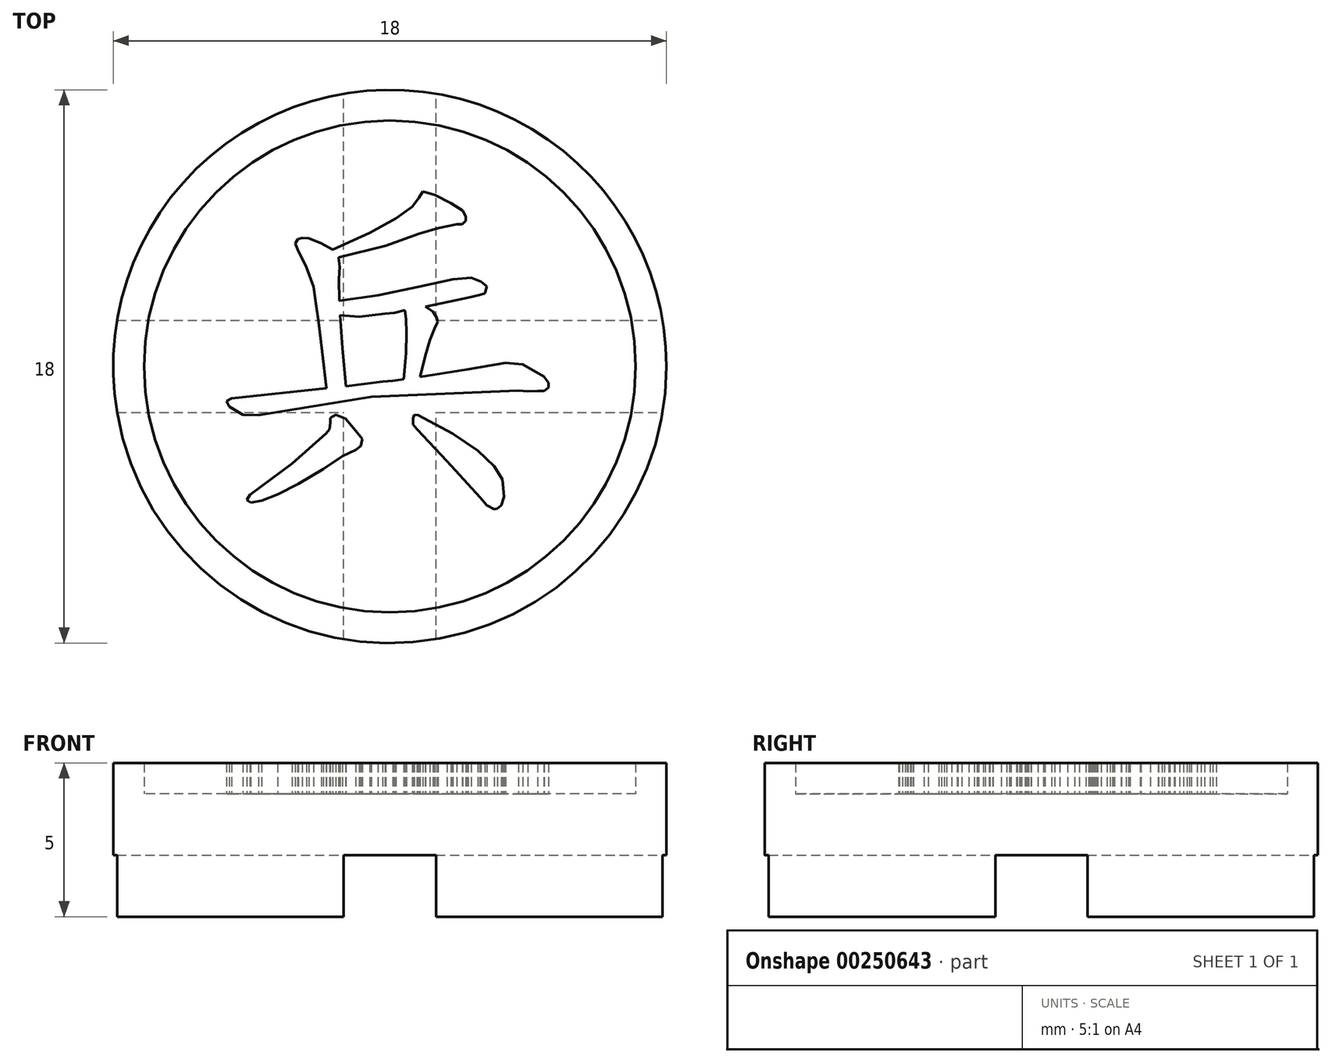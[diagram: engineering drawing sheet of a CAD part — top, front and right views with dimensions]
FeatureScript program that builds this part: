
annotation { "Feature Type Name" : "Feature", "Feature Type Description" : "" }
export const myFeature = defineFeature(function(context is Context, id is Id, definition is map)
    precondition{}
    {
        {
            var Q0;
            Q0=qCreatedBy(makeId("Top.planeOp"),FACE);
            var sketch = newSketch(context, id + "F0", { "sketchPlane" : qUnion([Q0])});
            skCircle(sketch, "E0", {"center": v(-31.33, 19.76) * mm, "radius": 9 * mm});
            skSolve(sketch);
        }
        {
            var Q0;
            Q0=qSketchRegion(id+"F0",true);
            extrude(context, id + "F1", {"entities" : qUnion([Q0]), "depth" : 4 * mm});
        }
        {
            var Q0;
            Q0=makeQuery(id+"F1.opExtrude","CAP_FACE",FACE,{"disambiguationData":[OSD([sQuery(id+"F0.wireOp",EDGE,"E0")])],"isStart":false});
            var sketch = newSketch(context, id + "F2", { "sketchPlane" : qUnion([Q0])});
            skCircle(sketch, "E1", {"center": v(-31.33, 19.76) * mm, "radius": 8 * mm});
            skCircle(sketch, "E2", {"center": v(-31.33, 19.76) * mm, "radius": 9 * mm});
            skSolve(sketch);
        }
        {
            var Q0;
            Q0=makeQuery(id+"F1.opExtrude","CAP_FACE",FACE,{"disambiguationData":[OSD([sQuery(id+"F0.wireOp",EDGE,"E0")])],"isStart":true});
            var sketch = newSketch(context, id + "F3", { "sketchPlane" : qUnion([Q0])});
            skLineSegment(sketch, "E3", {"start": v(-31.33, -19.76) * mm, "end": v(-22.33, -19.76) * mm, "construction": true});
            skLineSegment(sketch, "E4", {"start": v(-31.33, -19.76) * mm, "end": v(-31.33, -10.76) * mm, "construction": true});
            skLineSegment(sketch, "E5", {"start": v(-31.33, -19.76) * mm, "end": v(-40.33, -19.76) * mm, "construction": true});
            skLineSegment(sketch, "E6", {"start": v(-31.33, -19.76) * mm, "end": v(-31.33, -28.76) * mm, "construction": true});
            skLineSegment(sketch, "E7.bottom", {"start": v(-40.33, -28.76) * mm, "end": v(-22.33, -28.76) * mm});
            skLineSegment(sketch, "E7.top", {"start": v(-40.33, -10.76) * mm, "end": v(-22.33, -10.76) * mm});
            skLineSegment(sketch, "E7.left", {"start": v(-22.33, -10.76) * mm, "end": v(-22.33, -28.76) * mm});
            skLineSegment(sketch, "E7.right", {"start": v(-40.33, -10.76) * mm, "end": v(-40.33, -28.76) * mm});
            skPoint(sketch, "E8", {"position": v(-31.33, -28.76) * mm});
            skPoint(sketch, "E9", {"position": v(-40.33, -19.76) * mm});
            skPoint(sketch, "E10", {"position": v(-22.33, -19.76) * mm});
            skPoint(sketch, "E11", {"position": v(-31.33, -10.76) * mm});
            skLineSegment(sketch, "E12.bottom", {"start": v(-32.83, -10.76) * mm, "end": v(-29.83, -10.76) * mm});
            skLineSegment(sketch, "E12.top", {"start": v(-32.83, -28.76) * mm, "end": v(-29.83, -28.76) * mm});
            skLineSegment(sketch, "E12.left", {"start": v(-32.83, -10.76) * mm, "end": v(-32.83, -28.76) * mm});
            skLineSegment(sketch, "E12.right", {"start": v(-29.83, -10.76) * mm, "end": v(-29.83, -28.76) * mm});
            skLineSegment(sketch, "E13.bottom", {"start": v(-40.33, -18.26) * mm, "end": v(-22.33, -18.26) * mm});
            skLineSegment(sketch, "E13.top", {"start": v(-40.33, -21.26) * mm, "end": v(-22.33, -21.26) * mm});
            skLineSegment(sketch, "E13.left", {"start": v(-40.33, -18.26) * mm, "end": v(-40.33, -21.26) * mm});
            skLineSegment(sketch, "E13.right", {"start": v(-22.33, -18.26) * mm, "end": v(-22.33, -21.26) * mm});
            skSolve(sketch);
        }
        {
            var Q0;
            {var subQ1=sQuery(id+"F3.wireOp",EDGE,"E12.bottom");var subQ3=makeQuery(id+"F1.opExtrude","CAP_EDGE",EDGE,{"disambiguationData":[OSD([sQuery(id+"F0.wireOp",EDGE,"E0")])],"isStart":true});var subQ4=makeQuery(id+"F3.imprint","INTERSECT",VERTEX,{"derivedFrom":[subQ3,subQ1]});Q0=makeQuery(id+"F3.imprint","IMPRINT",FACE,{"disambiguationData":[TD([[makeQuery(id+"F3.imprint","IMPRINT",EDGE,{"disambiguationData":[TD([[subQ4,1.0]])],"derivedFrom":subQ3}),1.0]])]});}
            var Q1;
            {var subQ1=sQuery(id+"F3.wireOp",EDGE,"E12.bottom");var subQ3=makeQuery(id+"F1.opExtrude","CAP_EDGE",EDGE,{"disambiguationData":[OSD([sQuery(id+"F0.wireOp",EDGE,"E0")])],"isStart":true});var subQ4=makeQuery(id+"F3.imprint","INTERSECT",VERTEX,{"derivedFrom":[subQ3,subQ1]});Q1=makeQuery(id+"F3.imprint","IMPRINT",FACE,{"disambiguationData":[TD([[makeQuery(id+"F3.imprint","IMPRINT",EDGE,{"disambiguationData":[TD([[subQ4,-1.0]])],"derivedFrom":subQ3}),1.0]])]});}
            var Q2;
            {var subQ1=sQuery(id+"F3.wireOp",EDGE,"E12.top");var subQ3=makeQuery(id+"F1.opExtrude","CAP_EDGE",EDGE,{"disambiguationData":[OSD([sQuery(id+"F0.wireOp",EDGE,"E0")])],"isStart":true});var subQ4=makeQuery(id+"F3.imprint","INTERSECT",VERTEX,{"derivedFrom":[subQ3,subQ1]});Q2=makeQuery(id+"F3.imprint","IMPRINT",FACE,{"disambiguationData":[TD([[makeQuery(id+"F3.imprint","IMPRINT",EDGE,{"disambiguationData":[TD([[subQ4,-1.0]])],"derivedFrom":subQ3}),1.0]])]});}
            var Q3;
            {var subQ1=sQuery(id+"F3.wireOp",EDGE,"E12.top");var subQ3=makeQuery(id+"F1.opExtrude","CAP_EDGE",EDGE,{"disambiguationData":[OSD([sQuery(id+"F0.wireOp",EDGE,"E0")])],"isStart":true});var subQ4=makeQuery(id+"F3.imprint","INTERSECT",VERTEX,{"derivedFrom":[subQ3,subQ1]});Q3=makeQuery(id+"F3.imprint","IMPRINT",FACE,{"disambiguationData":[TD([[makeQuery(id+"F3.imprint","IMPRINT",EDGE,{"disambiguationData":[TD([[subQ4,1.0]])],"derivedFrom":subQ3}),1.0]])]});}
            var Q4;
            {var subQ0=sQuery(id+"F3.wireOp",EDGE,"E13.left");var subQ3=makeQuery(id+"F1.opExtrude","CAP_EDGE",EDGE,{"disambiguationData":[OSD([sQuery(id+"F0.wireOp",EDGE,"E0")])],"isStart":true});var subQ5=makeQuery(id+"F3.imprint","INTERSECT",VERTEX,{"derivedFrom":[subQ3,subQ0]});Q4=makeQuery(id+"F3.imprint","IMPRINT",FACE,{"disambiguationData":[TD([[makeQuery(id+"F3.imprint","IMPRINT",EDGE,{"disambiguationData":[TD([[subQ5,-1.0]])],"derivedFrom":subQ3}),1.0]])]});}
            var Q5;
            {var subQ0=sQuery(id+"F3.wireOp",EDGE,"E13.right");var subQ3=makeQuery(id+"F1.opExtrude","CAP_EDGE",EDGE,{"disambiguationData":[OSD([sQuery(id+"F0.wireOp",EDGE,"E0")])],"isStart":true});var subQ5=makeQuery(id+"F3.imprint","INTERSECT",VERTEX,{"derivedFrom":[subQ3,subQ0]});Q5=makeQuery(id+"F3.imprint","IMPRINT",FACE,{"disambiguationData":[TD([[makeQuery(id+"F3.imprint","IMPRINT",EDGE,{"disambiguationData":[TD([[subQ5,1.0]])],"derivedFrom":subQ3}),1.0]])]});}
            var Q6;
            {var subQ0=sQuery(id+"F3.wireOp",EDGE,"E13.left");var subQ3=makeQuery(id+"F1.opExtrude","CAP_EDGE",EDGE,{"disambiguationData":[OSD([sQuery(id+"F0.wireOp",EDGE,"E0")])],"isStart":true});var subQ5=makeQuery(id+"F3.imprint","INTERSECT",VERTEX,{"derivedFrom":[subQ3,subQ0]});Q6=makeQuery(id+"F3.imprint","IMPRINT",FACE,{"disambiguationData":[TD([[makeQuery(id+"F3.imprint","IMPRINT",EDGE,{"disambiguationData":[TD([[subQ5,1.0]])],"derivedFrom":subQ3}),1.0]])]});}
            var Q7;
            {var subQ0=sQuery(id+"F3.wireOp",EDGE,"E13.right");var subQ3=makeQuery(id+"F1.opExtrude","CAP_EDGE",EDGE,{"disambiguationData":[OSD([sQuery(id+"F0.wireOp",EDGE,"E0")])],"isStart":true});var subQ5=makeQuery(id+"F3.imprint","INTERSECT",VERTEX,{"derivedFrom":[subQ3,subQ0]});Q7=makeQuery(id+"F3.imprint","IMPRINT",FACE,{"disambiguationData":[TD([[makeQuery(id+"F3.imprint","IMPRINT",EDGE,{"disambiguationData":[TD([[subQ5,-1.0]])],"derivedFrom":subQ3}),1.0]])]});}
            var Q8;
            {var subQ3=makeQuery(id+"F1.opExtrude","CAP_EDGE",EDGE,{"disambiguationData":[OSD([sQuery(id+"F0.wireOp",EDGE,"E0")])],"isStart":true});var subQ5=sQuery(id+"F3.wireOp",EDGE,"E12.left");var subQ8=makeQuery(id+"F3.imprint","INTERSECT",VERTEX,{"disambiguationData":[OD(1.0)],"derivedFrom":[subQ3,subQ5]});Q8=makeQuery(id+"F3.imprint","IMPRINT",FACE,{"disambiguationData":[TD([[makeQuery(id+"F3.imprint","IMPRINT",EDGE,{"disambiguationData":[TD([[subQ8,-1.0]])],"derivedFrom":subQ3}),1.0]])]});}
            var Q9;
            {var subQ3=makeQuery(id+"F1.opExtrude","CAP_EDGE",EDGE,{"disambiguationData":[OSD([sQuery(id+"F0.wireOp",EDGE,"E0")])],"isStart":true});var subQ5=sQuery(id+"F3.wireOp",EDGE,"E12.right");var subQ8=makeQuery(id+"F3.imprint","INTERSECT",VERTEX,{"disambiguationData":[OD(1.0)],"derivedFrom":[subQ3,subQ5]});Q9=makeQuery(id+"F3.imprint","IMPRINT",FACE,{"disambiguationData":[TD([[makeQuery(id+"F3.imprint","IMPRINT",EDGE,{"disambiguationData":[TD([[subQ8,1.0]])],"derivedFrom":subQ3}),1.0]])]});}
            var Q10;
            {var subQ3=makeQuery(id+"F1.opExtrude","CAP_EDGE",EDGE,{"disambiguationData":[OSD([sQuery(id+"F0.wireOp",EDGE,"E0")])],"isStart":true});var subQ5=sQuery(id+"F3.wireOp",EDGE,"E12.left");var subQ8=makeQuery(id+"F3.imprint","INTERSECT",VERTEX,{"disambiguationData":[OD(0.0)],"derivedFrom":[subQ3,subQ5]});Q10=makeQuery(id+"F3.imprint","IMPRINT",FACE,{"disambiguationData":[TD([[makeQuery(id+"F3.imprint","IMPRINT",EDGE,{"disambiguationData":[TD([[subQ8,1.0]])],"derivedFrom":subQ3}),1.0]])]});}
            var Q11;
            {var subQ3=makeQuery(id+"F1.opExtrude","CAP_EDGE",EDGE,{"disambiguationData":[OSD([sQuery(id+"F0.wireOp",EDGE,"E0")])],"isStart":true});var subQ5=sQuery(id+"F3.wireOp",EDGE,"E12.right");var subQ8=makeQuery(id+"F3.imprint","INTERSECT",VERTEX,{"disambiguationData":[OD(0.0)],"derivedFrom":[subQ3,subQ5]});Q11=makeQuery(id+"F3.imprint","IMPRINT",FACE,{"disambiguationData":[TD([[makeQuery(id+"F3.imprint","IMPRINT",EDGE,{"disambiguationData":[TD([[subQ8,-1.0]])],"derivedFrom":subQ3}),1.0]])]});}
            var Q12;
            {var subQ2=sQuery(id+"F3.wireOp",EDGE,"E12.left");var subQ4=sQuery(id+"F3.wireOp",EDGE,"E13.bottom");var subQ8=makeQuery(id+"F3.imprint","INTERSECT",VERTEX,{"derivedFrom":[subQ2,subQ4]});Q12=makeQuery(id+"F3.imprint","IMPRINT",FACE,{"disambiguationData":[TD([[makeQuery(id+"F3.imprint","IMPRINT",EDGE,{"disambiguationData":[TD([[subQ8,1.0]])],"derivedFrom":subQ2}),1.0]])]});}
            var Q13;
            {var subQ1=sQuery(id+"F3.wireOp",EDGE,"E12.left");var subQ5=sQuery(id+"F3.wireOp",EDGE,"E13.bottom");var subQ6=makeQuery(id+"F3.imprint","INTERSECT",VERTEX,{"derivedFrom":[subQ1,subQ5]});Q13=makeQuery(id+"F3.imprint","IMPRINT",FACE,{"disambiguationData":[TD([[makeQuery(id+"F3.imprint","IMPRINT",EDGE,{"disambiguationData":[TD([[subQ6,-1.0]])],"derivedFrom":subQ1}),-1.0]])]});}
            var Q14;
            {var subQ0=sQuery(id+"F3.wireOp",EDGE,"E13.top");var subQ1=sQuery(id+"F3.wireOp",EDGE,"E12.left");var subQ2=makeQuery(id+"F3.imprint","INTERSECT",VERTEX,{"derivedFrom":[subQ1,subQ0]});Q14=makeQuery(id+"F3.imprint","IMPRINT",FACE,{"disambiguationData":[TD([[makeQuery(id+"F3.imprint","IMPRINT",EDGE,{"disambiguationData":[TD([[subQ2,-1.0]])],"derivedFrom":subQ1}),1.0]])]});}
            var Q15;
            {var subQ2=sQuery(id+"F3.wireOp",EDGE,"E13.bottom");var subQ5=sQuery(id+"F3.wireOp",EDGE,"E12.right");var subQ8=makeQuery(id+"F3.imprint","INTERSECT",VERTEX,{"derivedFrom":[subQ5,subQ2]});Q15=makeQuery(id+"F3.imprint","IMPRINT",FACE,{"disambiguationData":[TD([[makeQuery(id+"F3.imprint","IMPRINT",EDGE,{"disambiguationData":[TD([[subQ8,-1.0]])],"derivedFrom":subQ5}),1.0]])]});}
            var Q16;
            {var subQ0=sQuery(id+"F3.wireOp",EDGE,"E13.bottom");var subQ1=sQuery(id+"F3.wireOp",EDGE,"E12.left");var subQ2=makeQuery(id+"F3.imprint","INTERSECT",VERTEX,{"derivedFrom":[subQ1,subQ0]});Q16=makeQuery(id+"F3.imprint","IMPRINT",FACE,{"disambiguationData":[TD([[makeQuery(id+"F3.imprint","IMPRINT",EDGE,{"disambiguationData":[TD([[subQ2,-1.0]])],"derivedFrom":subQ1}),1.0]])]});}
            extrude(context, id + "F4", {"entities" : qUnion([Q0, Q1, Q2, Q3, Q4, Q5, Q6, Q7, Q8, Q9, Q10, Q11, Q12, Q13, Q14, Q15, Q16]), "operationType" : NewBodyOperationType.REMOVE, "oppositeDirection" : true, "depth" : 2 * mm});
        }
        {
            var Q0;
            Q0=qSketchRegion(id+"F2",true);
            var Q1;
            Q1=makeQuery(id+"F2.imprint","IMPRINT",FACE,{"disambiguationData":[TD([[makeQuery(id+"F2.imprint","IMPRINT",EDGE,{"derivedFrom":sQuery(id+"F2.wireOp",EDGE,"hKqnuJLd-dfdz-vJIs-yDKo-c4hLNRw30SuP")}),-1.0]])]});
            extrude(context, id + "F5", {"entities" : qUnion([Q0, Q1]), "operationType" : NewBodyOperationType.ADD, "depth" : 1 * mm});
        }
        {
            var Q0;
            Q0=makeQuery(id+"F1.opExtrude","CAP_FACE",FACE,{"disambiguationData":[OSD([sQuery(id+"F0.wireOp",EDGE,"E0")])],"isStart":false});
            var sketch = newSketch(context, id + "F6", { "sketchPlane" : qUnion([Q0])});
            skLineSegment(sketch, "E14", {"start": v(-33.39, 19.05) * mm, "end": v(-36.48, 18.72) * mm});
            skLineSegment(sketch, "E15", {"start": v(-36.48, 18.72) * mm, "end": v(-36.65, 18.63) * mm});
            skLineSegment(sketch, "E16", {"start": v(-36.65, 18.63) * mm, "end": v(-36.55, 18.46) * mm});
            skLineSegment(sketch, "E17", {"start": v(-36.55, 18.46) * mm, "end": v(-36.12, 18.18) * mm});
            skLineSegment(sketch, "E18", {"start": v(-36.12, 18.18) * mm, "end": v(-35.6, 18.17) * mm});
            skLineSegment(sketch, "E19", {"start": v(-35.6, 18.17) * mm, "end": v(-31.94, 18.77) * mm});
            skLineSegment(sketch, "E20", {"start": v(-31.94, 18.77) * mm, "end": v(-27.15, 18.97) * mm});
            skLineSegment(sketch, "E21", {"start": v(-27.15, 18.97) * mm, "end": v(-26.84, 18.95) * mm});
            skLineSegment(sketch, "E22", {"start": v(-26.84, 18.95) * mm, "end": v(-26.52, 18.96) * mm});
            skLineSegment(sketch, "E23", {"start": v(-26.52, 18.96) * mm, "end": v(-26.3, 18.96) * mm});
            skLineSegment(sketch, "E24", {"start": v(-26.3, 18.96) * mm, "end": v(-26.17, 19.07) * mm});
            skLineSegment(sketch, "E25", {"start": v(-26.17, 19.07) * mm, "end": v(-26.17, 19.23) * mm});
            skLineSegment(sketch, "E26", {"start": v(-26.17, 19.23) * mm, "end": v(-26.32, 19.43) * mm});
            skLineSegment(sketch, "E27", {"start": v(-26.32, 19.43) * mm, "end": v(-27, 19.82) * mm});
            skLineSegment(sketch, "E28", {"start": v(-27, 19.82) * mm, "end": v(-27.56, 19.88) * mm});
            skLineSegment(sketch, "E29", {"start": v(-27.56, 19.88) * mm, "end": v(-28.82, 19.65) * mm});
            skLineSegment(sketch, "E30", {"start": v(-28.82, 19.65) * mm, "end": v(-30.35, 19.41) * mm});
            skLineSegment(sketch, "E31", {"start": v(-30.35, 19.41) * mm, "end": v(-30.19, 20.1) * mm});
            skLineSegment(sketch, "E32", {"start": v(-30.19, 20.1) * mm, "end": v(-30.02, 20.62) * mm});
            skLineSegment(sketch, "E33", {"start": v(-30.02, 20.62) * mm, "end": v(-29.88, 20.99) * mm});
            skLineSegment(sketch, "E34", {"start": v(-29.88, 20.99) * mm, "end": v(-29.77, 21.21) * mm});
            skLineSegment(sketch, "E35", {"start": v(-29.77, 21.21) * mm, "end": v(-29.8, 21.34) * mm});
            skLineSegment(sketch, "E36", {"start": v(-29.8, 21.34) * mm, "end": v(-29.92, 21.54) * mm});
            skLineSegment(sketch, "E37", {"start": v(-29.92, 21.54) * mm, "end": v(-30.16, 21.7) * mm});
            skLineSegment(sketch, "E38", {"start": v(-30.16, 21.7) * mm, "end": v(-29.38, 21.87) * mm});
            skLineSegment(sketch, "E39", {"start": v(-29.38, 21.87) * mm, "end": v(-28.78, 22) * mm});
            skLineSegment(sketch, "E40", {"start": v(-28.78, 22) * mm, "end": v(-28.4, 22.09) * mm});
            skLineSegment(sketch, "E41", {"start": v(-28.4, 22.09) * mm, "end": v(-28.24, 22.14) * mm});
            skLineSegment(sketch, "E42", {"start": v(-28.24, 22.14) * mm, "end": v(-28.18, 22.36) * mm});
            skLineSegment(sketch, "E43", {"start": v(-28.18, 22.36) * mm, "end": v(-28.36, 22.51) * mm});
            skLineSegment(sketch, "E44", {"start": v(-28.36, 22.51) * mm, "end": v(-28.68, 22.65) * mm});
            skLineSegment(sketch, "E45", {"start": v(-28.68, 22.65) * mm, "end": v(-29.28, 22.6) * mm});
            skLineSegment(sketch, "E46", {"start": v(-29.28, 22.6) * mm, "end": v(-30.39, 22.35) * mm});
            skLineSegment(sketch, "E47", {"start": v(-30.39, 22.35) * mm, "end": v(-31.71, 22.08) * mm});
            skLineSegment(sketch, "E48", {"start": v(-31.71, 22.08) * mm, "end": v(-32.97, 21.9) * mm});
            skLineSegment(sketch, "E49", {"start": v(-32.97, 21.9) * mm, "end": v(-32.99, 22.6) * mm});
            skLineSegment(sketch, "E50", {"start": v(-32.99, 22.6) * mm, "end": v(-32.96, 23) * mm});
            skLineSegment(sketch, "E51", {"start": v(-32.96, 23) * mm, "end": v(-33, 23.3) * mm});
            skLineSegment(sketch, "E52", {"start": v(-33, 23.3) * mm, "end": v(-31.46, 23.69) * mm});
            skLineSegment(sketch, "E53", {"start": v(-31.46, 23.69) * mm, "end": v(-30.37, 24.08) * mm});
            skLineSegment(sketch, "E54", {"start": v(-30.37, 24.08) * mm, "end": v(-29.77, 24.26) * mm});
            skLineSegment(sketch, "E55", {"start": v(-29.77, 24.26) * mm, "end": v(-29.16, 24.38) * mm});
            skLineSegment(sketch, "E56", {"start": v(-29.16, 24.38) * mm, "end": v(-28.98, 24.39) * mm});
            skLineSegment(sketch, "E57", {"start": v(-28.98, 24.39) * mm, "end": v(-28.86, 24.5) * mm});
            skLineSegment(sketch, "E58", {"start": v(-28.86, 24.5) * mm, "end": v(-28.86, 24.64) * mm});
            skLineSegment(sketch, "E59", {"start": v(-28.86, 24.64) * mm, "end": v(-28.96, 24.83) * mm});
            skLineSegment(sketch, "E60", {"start": v(-28.96, 24.83) * mm, "end": v(-29.34, 25.07) * mm});
            skLineSegment(sketch, "E61", {"start": v(-29.34, 25.07) * mm, "end": v(-29.86, 25.34) * mm});
            skLineSegment(sketch, "E62", {"start": v(-29.86, 25.34) * mm, "end": v(-30.26, 25.45) * mm});
            skLineSegment(sketch, "E63", {"start": v(-30.26, 25.45) * mm, "end": v(-30.39, 25.25) * mm});
            skLineSegment(sketch, "E64", {"start": v(-30.39, 25.25) * mm, "end": v(-30.6, 24.95) * mm});
            skLineSegment(sketch, "E65", {"start": v(-30.6, 24.95) * mm, "end": v(-31.13, 24.57) * mm});
            skLineSegment(sketch, "E66", {"start": v(-31.13, 24.57) * mm, "end": v(-31.99, 24.1) * mm});
            skLineSegment(sketch, "E67", {"start": v(-31.99, 24.1) * mm, "end": v(-33.19, 23.55) * mm});
            skLineSegment(sketch, "E68", {"start": v(-33.19, 23.55) * mm, "end": v(-33.56, 23.76) * mm});
            skLineSegment(sketch, "E69", {"start": v(-33.56, 23.76) * mm, "end": v(-33.97, 23.93) * mm});
            skLineSegment(sketch, "E70", {"start": v(-33.97, 23.93) * mm, "end": v(-34.18, 23.94) * mm});
            skLineSegment(sketch, "E71", {"start": v(-34.18, 23.94) * mm, "end": v(-34.32, 23.9) * mm});
            skLineSegment(sketch, "E72", {"start": v(-34.32, 23.9) * mm, "end": v(-34.4, 23.76) * mm});
            skLineSegment(sketch, "E73", {"start": v(-34.4, 23.76) * mm, "end": v(-34.33, 23.57) * mm});
            skLineSegment(sketch, "E74", {"start": v(-34.33, 23.57) * mm, "end": v(-34.05, 22.97) * mm});
            skLineSegment(sketch, "E75", {"start": v(-34.05, 22.97) * mm, "end": v(-33.82, 22.35) * mm});
            skLineSegment(sketch, "E76", {"start": v(-33.82, 22.35) * mm, "end": v(-33.75, 21.9) * mm});
            skLineSegment(sketch, "E77", {"start": v(-33.75, 21.9) * mm, "end": v(-33.65, 21.2) * mm});
            skLineSegment(sketch, "E78", {"start": v(-33.65, 21.2) * mm, "end": v(-33.53, 20.25) * mm});
            skLineSegment(sketch, "E79", {"start": v(-33.53, 20.25) * mm, "end": v(-33.39, 19.05) * mm});
            skLineSegment(sketch, "E80", {"start": v(-31.57, 19.26) * mm, "end": v(-32.76, 19.11) * mm});
            skLineSegment(sketch, "E81", {"start": v(-32.76, 19.11) * mm, "end": v(-32.88, 20.36) * mm});
            skLineSegment(sketch, "E82", {"start": v(-32.88, 20.36) * mm, "end": v(-32.95, 21.42) * mm});
            skLineSegment(sketch, "E83", {"start": v(-32.95, 21.42) * mm, "end": v(-32.33, 21.38) * mm});
            skLineSegment(sketch, "E84", {"start": v(-32.33, 21.38) * mm, "end": v(-31.5, 21.47) * mm});
            skLineSegment(sketch, "E85", {"start": v(-31.5, 21.47) * mm, "end": v(-31.19, 21.5) * mm});
            skLineSegment(sketch, "E86", {"start": v(-31.19, 21.5) * mm, "end": v(-30.84, 21.59) * mm});
            skLineSegment(sketch, "E87", {"start": v(-30.84, 21.59) * mm, "end": v(-30.8, 21.3) * mm});
            skLineSegment(sketch, "E88", {"start": v(-30.8, 21.3) * mm, "end": v(-30.79, 20.84) * mm});
            skLineSegment(sketch, "E89", {"start": v(-30.79, 20.84) * mm, "end": v(-30.8, 20.2) * mm});
            skLineSegment(sketch, "E90", {"start": v(-30.8, 20.2) * mm, "end": v(-30.88, 19.35) * mm});
            skLineSegment(sketch, "E91", {"start": v(-30.88, 19.35) * mm, "end": v(-31.23, 19.3) * mm});
            skLineSegment(sketch, "E92", {"start": v(-31.23, 19.3) * mm, "end": v(-31.57, 19.26) * mm});
            skLineSegment(sketch, "E93", {"start": v(-33.4, 17.58) * mm, "end": v(-34.5, 16.6) * mm});
            skLineSegment(sketch, "E94", {"start": v(-34.5, 16.6) * mm, "end": v(-35.89, 15.58) * mm});
            skLineSegment(sketch, "E95", {"start": v(-35.89, 15.58) * mm, "end": v(-35.98, 15.42) * mm});
            skLineSegment(sketch, "E96", {"start": v(-35.98, 15.42) * mm, "end": v(-35.86, 15.33) * mm});
            skLineSegment(sketch, "E97", {"start": v(-35.86, 15.33) * mm, "end": v(-35.5, 15.39) * mm});
            skLineSegment(sketch, "E98", {"start": v(-35.5, 15.39) * mm, "end": v(-34.98, 15.6) * mm});
            skLineSegment(sketch, "E99", {"start": v(-34.98, 15.6) * mm, "end": v(-34.3, 15.94) * mm});
            skLineSegment(sketch, "E100", {"start": v(-34.3, 15.94) * mm, "end": v(-33.49, 16.42) * mm});
            skLineSegment(sketch, "E101", {"start": v(-33.49, 16.42) * mm, "end": v(-32.87, 16.85) * mm});
            skLineSegment(sketch, "E102", {"start": v(-32.87, 16.85) * mm, "end": v(-32.44, 17.05) * mm});
            skLineSegment(sketch, "E103", {"start": v(-32.44, 17.05) * mm, "end": v(-32.28, 17.17) * mm});
            skLineSegment(sketch, "E104", {"start": v(-32.28, 17.17) * mm, "end": v(-32.23, 17.4) * mm});
            skLineSegment(sketch, "E105", {"start": v(-32.23, 17.4) * mm, "end": v(-32.44, 17.67) * mm});
            skLineSegment(sketch, "E106", {"start": v(-32.44, 17.67) * mm, "end": v(-32.77, 18.06) * mm});
            skLineSegment(sketch, "E107", {"start": v(-32.77, 18.06) * mm, "end": v(-33.09, 18.18) * mm});
            skLineSegment(sketch, "E108", {"start": v(-33.09, 18.18) * mm, "end": v(-33.26, 18.1) * mm});
            skLineSegment(sketch, "E109", {"start": v(-33.26, 18.1) * mm, "end": v(-33.26, 17.93) * mm});
            skLineSegment(sketch, "E110", {"start": v(-33.26, 17.93) * mm, "end": v(-33.3, 17.72) * mm});
            skLineSegment(sketch, "E111", {"start": v(-33.3, 17.72) * mm, "end": v(-33.4, 17.58) * mm});
            skLineSegment(sketch, "E112", {"start": v(-30.45, 17.72) * mm, "end": v(-29.47, 16.68) * mm});
            skLineSegment(sketch, "E113", {"start": v(-29.47, 16.68) * mm, "end": v(-28.4, 15.5) * mm});
            skLineSegment(sketch, "E114", {"start": v(-28.4, 15.5) * mm, "end": v(-28.18, 15.25) * mm});
            skLineSegment(sketch, "E115", {"start": v(-28.18, 15.25) * mm, "end": v(-27.94, 15.11) * mm});
            skLineSegment(sketch, "E116", {"start": v(-27.94, 15.11) * mm, "end": v(-27.83, 15.13) * mm});
            skLineSegment(sketch, "E117", {"start": v(-27.83, 15.13) * mm, "end": v(-27.7, 15.24) * mm});
            skLineSegment(sketch, "E118", {"start": v(-27.7, 15.24) * mm, "end": v(-27.61, 15.52) * mm});
            skLineSegment(sketch, "E119", {"start": v(-27.61, 15.52) * mm, "end": v(-27.66, 16.08) * mm});
            skLineSegment(sketch, "E120", {"start": v(-27.66, 16.08) * mm, "end": v(-27.93, 16.51) * mm});
            skLineSegment(sketch, "E121", {"start": v(-27.93, 16.51) * mm, "end": v(-28.47, 17.01) * mm});
            skLineSegment(sketch, "E122", {"start": v(-28.47, 17.01) * mm, "end": v(-29.29, 17.57) * mm});
            skLineSegment(sketch, "E123", {"start": v(-29.29, 17.57) * mm, "end": v(-30.41, 18.17) * mm});
            skLineSegment(sketch, "E124", {"start": v(-30.41, 18.17) * mm, "end": v(-30.53, 18.19) * mm});
            skLineSegment(sketch, "E125", {"start": v(-30.53, 18.19) * mm, "end": v(-30.57, 18.07) * mm});
            skLineSegment(sketch, "E126", {"start": v(-30.57, 18.07) * mm, "end": v(-30.57, 17.87) * mm});
            skLineSegment(sketch, "E127", {"start": v(-30.57, 17.87) * mm, "end": v(-30.45, 17.72) * mm});
            skSolve(sketch);
        }
        {
            var Q0;
            Q0 = qSketchRegion(id + "F6", true);
            extrude(context, id + "F7", {"entities" : qUnion([Q0]), "operationType" : NewBodyOperationType.ADD, "depth" : 1 * mm, "offsetDistance" : 25 * mm});
        }
    });
